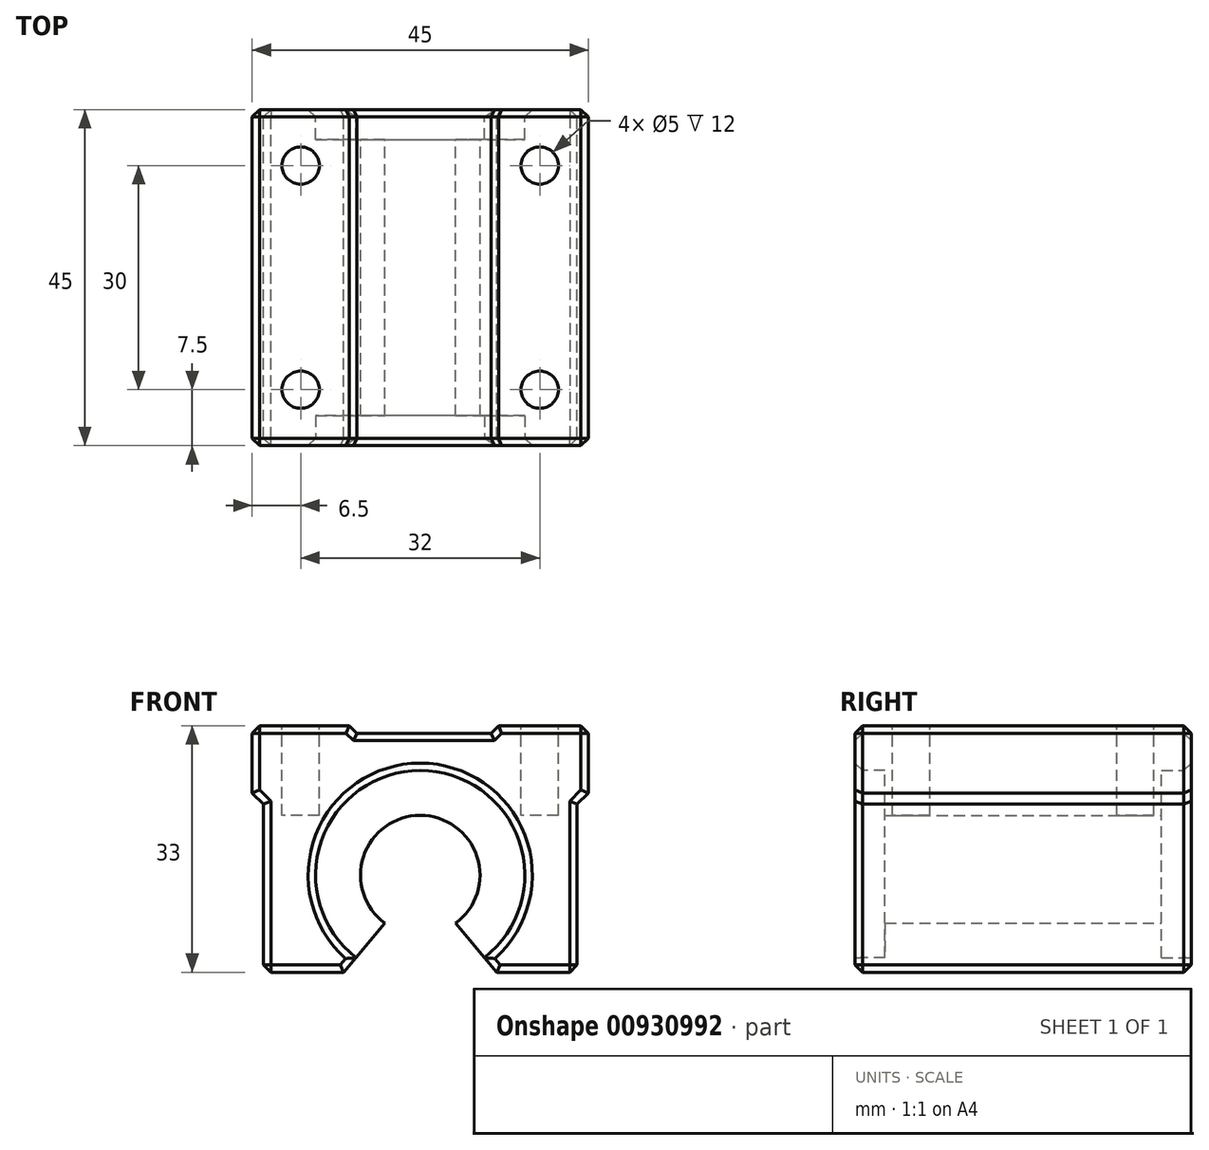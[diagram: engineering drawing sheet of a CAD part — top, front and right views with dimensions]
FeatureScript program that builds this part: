
annotation { "Feature Type Name" : "Feature", "Feature Type Description" : "" }
export const myFeature = defineFeature(function(context is Context, id is Id, definition is map)
    precondition{}
    {
        {
            var Q0;
            Q0=qCreatedBy(makeId("Front.planeOp"),FACE);
            var sketch = newSketch(context, id + "F0", { "sketchPlane" : qUnion([Q0])});
            skLineSegment(sketch, "E0.bottom", {"start": v(0, 0) * mm, "end": v(22.5, 0) * mm, "construction": true});
            skLineSegment(sketch, "E0.top", {"start": v(0, 33) * mm, "end": v(13, 33) * mm});
            skLineSegment(sketch, "E0.left", {"start": v(0, 0) * mm, "end": v(0, 33) * mm, "construction": true});
            skLineSegment(sketch, "E0.right", {"start": v(22.5, 0) * mm, "end": v(22.5, 33) * mm, "construction": true});
            skLineSegment(sketch, "E1", {"start": v(1.5, 22.5) * mm, "end": v(1.5, 0) * mm});
            skLineSegment(sketch, "E2", {"start": v(1.5, 22.5) * mm, "end": v(0, 24) * mm});
            skLineSegment(sketch, "E3", {"start": v(0, 33) * mm, "end": v(0, 24) * mm});
            skArc(sketch, "E4", {"start": v(22.5, 21) * mm, "mid": v(14.9, 15.5) * mm, "end": v(17.75, 6.56) * mm});
            skLineSegment(sketch, "E5.MirrorCS", {"start": v(45, 33) * mm, "end": v(33, 33) * mm});
            skLineSegment(sketch, "E6.MirrorCS", {"start": v(45, 33) * mm, "end": v(45, 24) * mm});
            skLineSegment(sketch, "E7.MirrorCS", {"start": v(43.5, 22.5) * mm, "end": v(43.5, 0) * mm});
            skArc(sketch, "E8.MirrorCS", {"start": v(22.5, 21) * mm, "mid": v(30.1, 15.5) * mm, "end": v(27.25, 6.56) * mm});
            skLineSegment(sketch, "E9.MirrorCS", {"start": v(43.5, 22.5) * mm, "end": v(45, 24) * mm});
            skLineSegment(sketch, "E10", {"start": v(33, 33) * mm, "end": v(33, 32) * mm, "construction": true});
            skLineSegment(sketch, "E11", {"start": v(32, 32) * mm, "end": v(14, 32) * mm});
            skLineSegment(sketch, "E12", {"start": v(13, 32) * mm, "end": v(13, 33) * mm, "construction": true});
            skLineSegment(sketch, "E13", {"start": v(13, 33) * mm, "end": v(14, 32) * mm});
            skLineSegment(sketch, "E14", {"start": v(33, 33) * mm, "end": v(32, 32) * mm});
            skLineSegment(sketch, "E15", {"start": v(13, 32) * mm, "end": v(33, 32) * mm, "construction": true});
            skPoint(sketch, "E16.orphan", {"position": v(22.5, 33) * mm});
            skLineSegment(sketch, "E17", {"start": v(17.75, 6.56) * mm, "end": v(12.25, 0) * mm});
            skLineSegment(sketch, "E18", {"start": v(12.25, 0) * mm, "end": v(1.5, 0) * mm});
            skLineSegment(sketch, "E19.MirrorCS", {"start": v(27.25, 6.56) * mm, "end": v(32.75, 0) * mm});
            skLineSegment(sketch, "E20.MirrorCS", {"start": v(32.75, 0) * mm, "end": v(43.5, 0) * mm});
            skSolve(sketch);
        }
        {
            var Q0;
            Q0 = qSketchRegion(id + "F0", true);
            extrude(context, id + "F1", {"entities" : qUnion([Q0]), "depth" : 45 * mm, "offsetDistance" : 25 * mm});
        }
        {
            var Q0;
            Q0=makeQuery(id+"F1.opExtrude","CAP_FACE",FACE,{"disambiguationData":[OSD([sQuery(id+"F0.wireOp",EDGE,"E0.top"),sQuery(id+"F0.wireOp",EDGE,"E1"),sQuery(id+"F0.wireOp",EDGE,"E2"),sQuery(id+"F0.wireOp",EDGE,"E3"),sQuery(id+"F0.wireOp",EDGE,"E4"),sQuery(id+"F0.wireOp",EDGE,"uqlTuz2a-mfTU-LUhv-xMSi-QFBtyIHp41u1"),sQuery(id+"F0.wireOp",EDGE,"ZgPj9IN8-vdyW-sj4Y-b42i-XJZkOsrtmJ2G"),sQuery(id+"F0.wireOp",EDGE,"E5.MirrorCS"),sQuery(id+"F0.wireOp",EDGE,"E6.MirrorCS"),sQuery(id+"F0.wireOp",EDGE,"E7.MirrorCS"),sQuery(id+"F0.wireOp",EDGE,"4d39c08c-c8aa-4ed0-84f7-bf6fc0a5b37b0.MirrorCS"),sQuery(id+"F0.wireOp",EDGE,"2afa55dc-c1fa-4448-ae93-07702a50ea040.MirrorCS"),sQuery(id+"F0.wireOp",EDGE,"E8.MirrorCS"),sQuery(id+"F0.wireOp",EDGE,"E9.MirrorCS"),sQuery(id+"F0.wireOp",EDGE,"E11"),sQuery(id+"F0.wireOp",EDGE,"E13"),sQuery(id+"F0.wireOp",EDGE,"E14")])],"isStart":false});
            var sketch = newSketch(context, id + "F2", { "sketchPlane" : qUnion([Q0])});
            skCircle(sketch, "E21", {"center": v(22.5, 13) * mm, "radius": 14 * mm});
            skSolve(sketch);
        }
        {
            var Q0;
            Q0 = qSketchRegion(id + "F2", true);
            extrude(context, id + "F3", {"entities" : qUnion([Q0]), "operationType" : NewBodyOperationType.REMOVE, "oppositeDirection" : true, "depth" : 4 * mm, "offsetDistance" : 25 * mm});
        }
        {
            var Q0;
            Q0=makeQuery(id+"F1.opExtrude","CAP_FACE",FACE,{"disambiguationData":[OSD([sQuery(id+"F0.wireOp",EDGE,"E0.top"),sQuery(id+"F0.wireOp",EDGE,"E1"),sQuery(id+"F0.wireOp",EDGE,"E2"),sQuery(id+"F0.wireOp",EDGE,"E3"),sQuery(id+"F0.wireOp",EDGE,"E4"),sQuery(id+"F0.wireOp",EDGE,"E5.MirrorCS"),sQuery(id+"F0.wireOp",EDGE,"E6.MirrorCS"),sQuery(id+"F0.wireOp",EDGE,"E7.MirrorCS"),sQuery(id+"F0.wireOp",EDGE,"E8.MirrorCS"),sQuery(id+"F0.wireOp",EDGE,"E9.MirrorCS"),sQuery(id+"F0.wireOp",EDGE,"E11"),sQuery(id+"F0.wireOp",EDGE,"E13"),sQuery(id+"F0.wireOp",EDGE,"E14"),sQuery(id+"F0.wireOp",EDGE,"E17"),sQuery(id+"F0.wireOp",EDGE,"E18"),sQuery(id+"F0.wireOp",EDGE,"E19.MirrorCS"),sQuery(id+"F0.wireOp",EDGE,"E20.MirrorCS")])],"isStart":true});
            var sketch = newSketch(context, id + "F4", { "sketchPlane" : qUnion([Q0])});
            skCircle(sketch, "E22", {"center": v(-22.5, 13) * mm, "radius": 14 * mm});
            skSolve(sketch);
        }
        {
            var Q0;
            Q0 = qSketchRegion(id + "F4", true);
            extrude(context, id + "F5", {"entities" : qUnion([Q0]), "operationType" : NewBodyOperationType.REMOVE, "oppositeDirection" : true, "depth" : 4 * mm, "offsetDistance" : 25 * mm});
        }
        {
            var Q0;
            Q0=makeQuery(id+"F1.opExtrude","SWEPT_FACE",FACE,{"disambiguationData":[OSD([sQuery(id+"F0.wireOp",EDGE,"E0.top")])]});
            var sketch = newSketch(context, id + "F6", { "sketchPlane" : qUnion([Q0])});
            skCircle(sketch, "E23", {"center": v(6.5, -37.5) * mm, "radius": 2.5 * mm});
            skLineSegment(sketch, "E24", {"start": v(0, -22.5) * mm, "end": v(45, -22.5) * mm, "construction": true});
            skLineSegment(sketch, "E25", {"start": v(22.5, -22.5) * mm, "end": v(22.5, -45) * mm, "construction": true});
            skCircle(sketch, "E26.MirrorC", {"center": v(38.5, -37.5) * mm, "radius": 2.5 * mm});
            skCircle(sketch, "E27.MirrorC", {"center": v(6.5, -7.5) * mm, "radius": 2.5 * mm});
            skCircle(sketch, "E28.MirrorC", {"center": v(38.5, -7.5) * mm, "radius": 2.5 * mm});
            skSolve(sketch);
        }
        {
            var Q0;
            Q0 = qSketchRegion(id + "F6", true);
            extrude(context, id + "F7", {"entities" : qUnion([Q0]), "operationType" : NewBodyOperationType.REMOVE, "oppositeDirection" : true, "depth" : 12 * mm, "offsetDistance" : 25 * mm});
        }
        {
            var Q0;
            Q0=makeQuery(id+"F1.opExtrude","CAP_FACE",FACE,{"disambiguationData":[OSD([sQuery(id+"F0.wireOp",EDGE,"E0.top"),sQuery(id+"F0.wireOp",EDGE,"E1"),sQuery(id+"F0.wireOp",EDGE,"E2"),sQuery(id+"F0.wireOp",EDGE,"E3"),sQuery(id+"F0.wireOp",EDGE,"E4"),sQuery(id+"F0.wireOp",EDGE,"E5.MirrorCS"),sQuery(id+"F0.wireOp",EDGE,"E6.MirrorCS"),sQuery(id+"F0.wireOp",EDGE,"E7.MirrorCS"),sQuery(id+"F0.wireOp",EDGE,"E8.MirrorCS"),sQuery(id+"F0.wireOp",EDGE,"E9.MirrorCS"),sQuery(id+"F0.wireOp",EDGE,"E11"),sQuery(id+"F0.wireOp",EDGE,"E13"),sQuery(id+"F0.wireOp",EDGE,"E14"),sQuery(id+"F0.wireOp",EDGE,"E17"),sQuery(id+"F0.wireOp",EDGE,"E18"),sQuery(id+"F0.wireOp",EDGE,"E19.MirrorCS"),sQuery(id+"F0.wireOp",EDGE,"E20.MirrorCS")])],"isStart":true});
            var Q1;
            Q1=makeQuery(id+"F1.opExtrude","CAP_FACE",FACE,{"disambiguationData":[OSD([sQuery(id+"F0.wireOp",EDGE,"E0.top"),sQuery(id+"F0.wireOp",EDGE,"E1"),sQuery(id+"F0.wireOp",EDGE,"E2"),sQuery(id+"F0.wireOp",EDGE,"E3"),sQuery(id+"F0.wireOp",EDGE,"E4"),sQuery(id+"F0.wireOp",EDGE,"E5.MirrorCS"),sQuery(id+"F0.wireOp",EDGE,"E6.MirrorCS"),sQuery(id+"F0.wireOp",EDGE,"E7.MirrorCS"),sQuery(id+"F0.wireOp",EDGE,"E8.MirrorCS"),sQuery(id+"F0.wireOp",EDGE,"E9.MirrorCS"),sQuery(id+"F0.wireOp",EDGE,"E11"),sQuery(id+"F0.wireOp",EDGE,"E13"),sQuery(id+"F0.wireOp",EDGE,"E14"),sQuery(id+"F0.wireOp",EDGE,"E17"),sQuery(id+"F0.wireOp",EDGE,"E18"),sQuery(id+"F0.wireOp",EDGE,"E19.MirrorCS"),sQuery(id+"F0.wireOp",EDGE,"E20.MirrorCS")])],"isStart":false});
            var Q2;
            Q2=makeQuery(id+"F1.opExtrude","SWEPT_EDGE",EDGE,{"disambiguationData":[OSD([sQuery(id+"F0.wireOp",EDGE,"E5.MirrorCS"),sQuery(id+"F0.wireOp",EDGE,"E6.MirrorCS")])]});
            var Q3;
            Q3=makeQuery(id+"F1.opExtrude","SWEPT_EDGE",EDGE,{"disambiguationData":[OSD([sQuery(id+"F0.wireOp",EDGE,"E0.top"),sQuery(id+"F0.wireOp",EDGE,"E3")])]});
            var Q4;
            Q4=makeQuery(id+"F1.opExtrude","SWEPT_EDGE",EDGE,{"disambiguationData":[OSD([sQuery(id+"F0.wireOp",EDGE,"E1"),sQuery(id+"F0.wireOp",EDGE,"E18")])]});
            var Q5;
            Q5=makeQuery(id+"F1.opExtrude","SWEPT_EDGE",EDGE,{"disambiguationData":[OSD([sQuery(id+"F0.wireOp",EDGE,"E7.MirrorCS"),sQuery(id+"F0.wireOp",EDGE,"E20.MirrorCS")])]});
            chamfer(context, id + "F8", {"entities" : qUnion([Q0, Q1, Q2, Q3, Q4, Q5]), "width" : 1 * mm, "tangentPropagation" : true});
        }
    });
